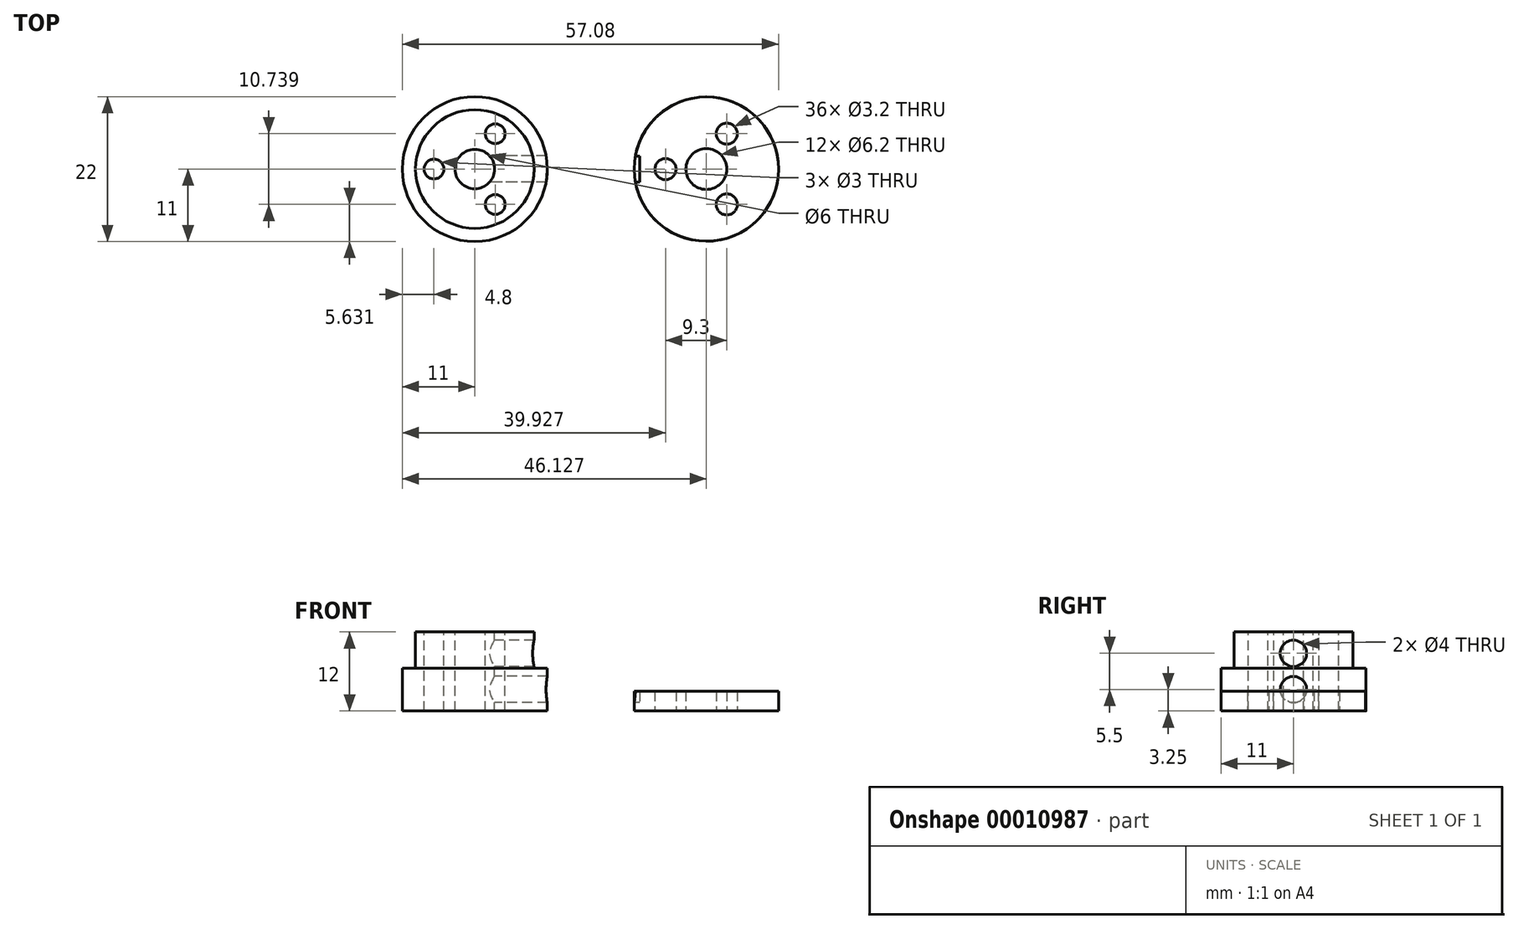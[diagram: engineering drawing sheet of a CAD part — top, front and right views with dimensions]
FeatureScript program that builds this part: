
annotation { "Feature Type Name" : "Feature", "Feature Type Description" : "" }
export const myFeature = defineFeature(function(context is Context, id is Id, definition is map)
    precondition{}
    {
        {
            var Q0;
            Q0=qCreatedBy(makeId("Top.planeOp"),FACE);
            var sketch = newSketch(context, id + "F0", { "sketchPlane" : qUnion([Q0])});
            skCircle(sketch, "E0", {"center": v(0, 0) * mm, "radius": 11 * mm});
            skSolve(sketch);
        }
        {
            var Q0;
            Q0=makeQuery(id+"F0.imprint","IMPRINT",FACE,{"disambiguationData":[TD([[makeQuery(id+"F0.imprint","IMPRINT",EDGE,{"derivedFrom":sQuery(id+"F0.wireOp",EDGE,"E0")}),1.0]])]});
            extrude(context, id + "F1", {"entities" : qUnion([Q0]), "depth" : 6.5 * mm});
        }
        {
            var Q0;
            Q0=makeQuery(id+"F1.opExtrude","CAP_FACE",FACE,{"disambiguationData":[OSD([sQuery(id+"F0.wireOp",EDGE,"E0")])],"isStart":false});
            var sketch = newSketch(context, id + "F2", { "sketchPlane" : qUnion([Q0])});
            skCircle(sketch, "E1", {"center": v(0, 0) * mm, "radius": 9 * mm});
            skSolve(sketch);
        }
        {
            var Q0;
            Q0=makeQuery(id+"F2.imprint","IMPRINT",FACE,{"disambiguationData":[TD([[makeQuery(id+"F2.imprint","IMPRINT",EDGE,{"derivedFrom":sQuery(id+"F2.wireOp",EDGE,"E1")}),1.0]])]});
            extrude(context, id + "F3", {"entities" : qUnion([Q0]), "operationType" : NewBodyOperationType.ADD, "depth" : 5.5 * mm});
        }
        {
            var Q0;
            Q0=makeQuery(id+"F3.opExtrude","CAP_FACE",FACE,{"disambiguationData":[OSD([sQuery(id+"F2.wireOp",EDGE,"E1")])],"isStart":false});
            var sketch = newSketch(context, id + "F4", { "sketchPlane" : qUnion([Q0])});
            skCircle(sketch, "E2", {"center": v(0, 0) * mm, "radius": 3 * mm});
            skCircle(sketch, "E3", {"center": v(3.1, 5.37) * mm, "radius": 1.5 * mm});
            skLineSegment(sketch, "E4", {"start": v(3.1, 5.37) * mm, "end": v(0, 0) * mm});
            skLineSegment(sketch, "E5", {"start": v(0, 0) * mm, "end": v(-5.23, 0) * mm});
            skCircle(sketch, "E6.1.0", {"center": v(3.1, -5.37) * mm, "radius": 1.5 * mm});
            skCircle(sketch, "E6.2.0", {"center": v(-6.2, 0) * mm, "radius": 1.5 * mm});
            skLineSegment(sketch, "E6.anchor1", {"start": v(0, 0) * mm, "end": v(3.1, 5.37) * mm, "construction": true});
            skLineSegment(sketch, "E6.anchor2", {"start": v(0, 0) * mm, "end": v(-6.2, 0) * mm, "construction": true});
            skSolve(sketch);
        }
        {
            var Q0;
            Q0 = qSketchRegion(id + "F4", true);
            extrude(context, id + "F5", {"entities" : qUnion([Q0]), "operationType" : NewBodyOperationType.REMOVE, "endBound" : BoundingType.THROUGH_ALL, "oppositeDirection" : true, "depth" : 25 * mm});
        }
        {
            var Q0;
            Q0=qCreatedBy(makeId("Right.planeOp"),FACE);
            var sketch = newSketch(context, id + "F6", { "sketchPlane" : qUnion([Q0])});
            skCircle(sketch, "E7", {"center": v(0, 8.75) * mm, "radius": 2 * mm});
            skCircle(sketch, "E8", {"center": v(0, 3.25) * mm, "radius": 2 * mm});
            skSolve(sketch);
        }
        {
            var Q0;
            Q0 = qSketchRegion(id + "F6", true);
            extrude(context, id + "F7", {"entities" : qUnion([Q0]), "operationType" : NewBodyOperationType.REMOVE, "depth" : 25 * mm});
        }
        {
            var Q0;
            Q0=qCreatedBy(makeId("Top.planeOp"),FACE);
            var sketch = newSketch(context, id + "F8", { "sketchPlane" : qUnion([Q0])});
            skCircle(sketch, "E9", {"center": v(35.13, 0) * mm, "radius": 10.95 * mm});
            skCircle(sketch, "E10", {"center": v(35.13, 0) * mm, "radius": 3.1 * mm});
            skCircle(sketch, "E11.1.0", {"center": v(38.23, -5.37) * mm, "radius": 1.6 * mm});
            skCircle(sketch, "E11.2.0", {"center": v(28.93, 0) * mm, "radius": 1.6 * mm});
            skLineSegment(sketch, "E12", {"start": v(35.13, 0) * mm, "end": v(29.8, 0) * mm});
            skCircle(sketch, "E13", {"center": v(38.23, 5.37) * mm, "radius": 1.6 * mm});
            skLineSegment(sketch, "E14", {"start": v(38.23, 5.37) * mm, "end": v(35.13, 0) * mm});
            skLineSegment(sketch, "E11.anchor2", {"start": v(35.13, 0) * mm, "end": v(28.93, 0) * mm, "construction": true});
            skLineSegment(sketch, "E11.anchor1", {"start": v(35.13, 0) * mm, "end": v(38.23, 5.37) * mm, "construction": true});
            skSolve(sketch);
        }
        {
            var Q0;
            Q0=makeQuery(id+"F8.imprint","IMPRINT",FACE,{"disambiguationData":[TD([[makeQuery(id+"F8.imprint","IMPRINT",EDGE,{"derivedFrom":sQuery(id+"F8.wireOp",EDGE,"E9")}),1.0]])]});
            extrude(context, id + "F9", {"entities" : qUnion([Q0]), "depth" : 3 * mm});
        }
    });
